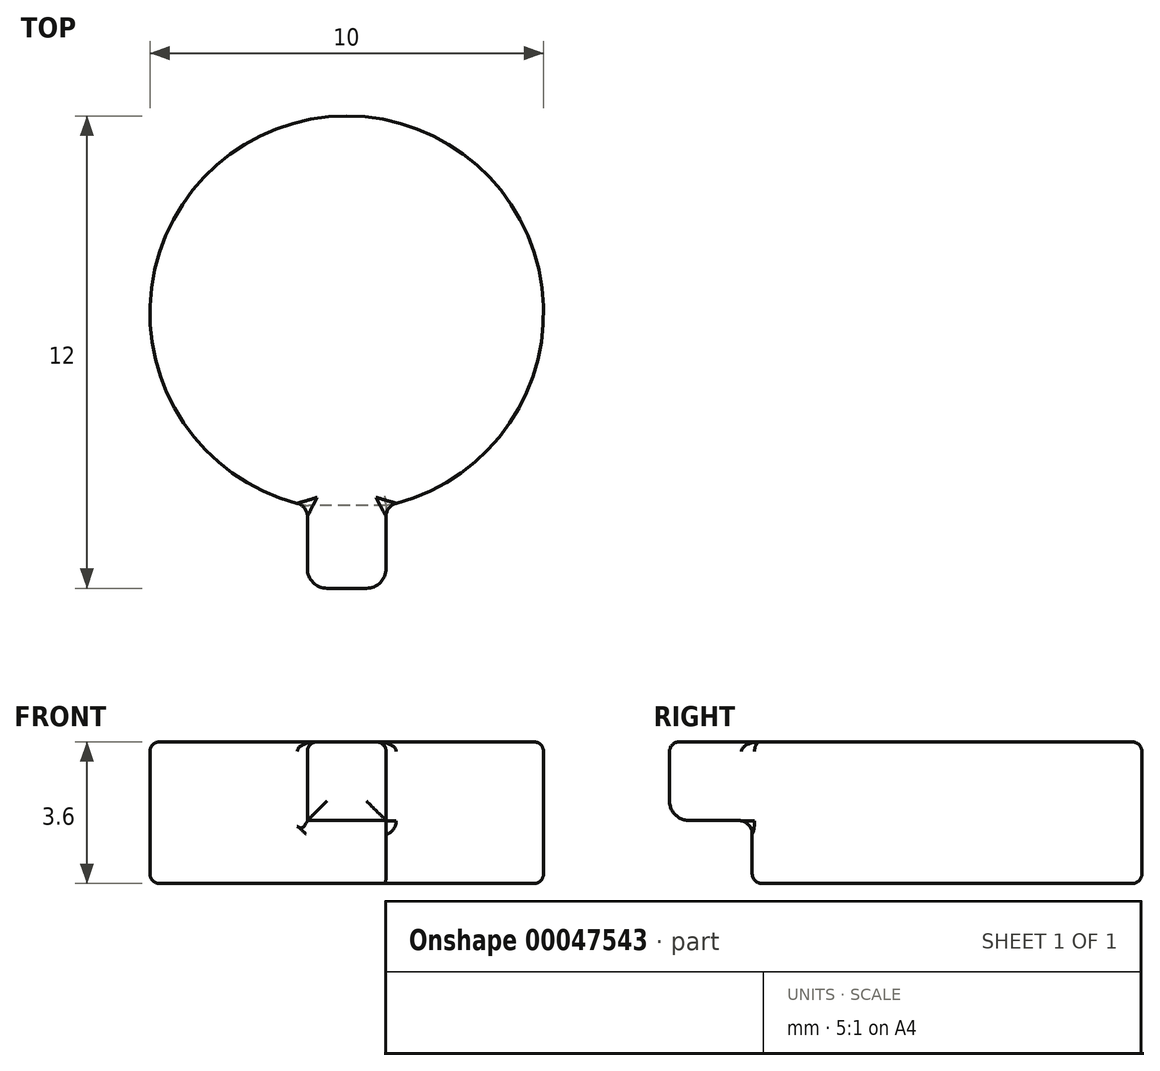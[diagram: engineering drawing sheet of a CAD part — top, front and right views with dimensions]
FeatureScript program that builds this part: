
annotation { "Feature Type Name" : "Feature", "Feature Type Description" : "" }
export const myFeature = defineFeature(function(context is Context, id is Id, definition is map)
    precondition{}
    {
        {
            var Q0;
            Q0=qCreatedBy(makeId("Top.planeOp"),FACE);
            var sketch = newSketch(context, id + "F0", { "sketchPlane" : qUnion([Q0])});
            skArc(sketch, "E0", {"start": v(1, -4.9) * mm, "mid": v(0, 5) * mm, "end": v(-1, -4.9) * mm});
            skLineSegment(sketch, "E1.top", {"start": v(-1, -7) * mm, "end": v(1, -7) * mm});
            skLineSegment(sketch, "E1.left", {"start": v(-1, -4.9) * mm, "end": v(-1, -7) * mm});
            skLineSegment(sketch, "E1.right", {"start": v(1, -4.9) * mm, "end": v(1, -7) * mm});
            skSolve(sketch);
        }
        {
            var Q0;
            Q0 = qSketchRegion(id + "F0", true);
            extrude(context, id + "F1", {"entities" : qUnion([Q0]), "depth" : 3.6 * mm});
        }
        {
            var Q0;
            Q0=makeQuery(id+"F1.opExtrude","SWEPT_FACE",FACE,{"disambiguationData":[OSD([sQuery(id+"F0.wireOp",EDGE,"E1.left")])]});
            var sketch = newSketch(context, id + "F2", { "sketchPlane" : qUnion([Q0])});
            skLineSegment(sketch, "E2.bottom", {"start": v(4.9, 0) * mm, "end": v(7, 0) * mm});
            skLineSegment(sketch, "E2.top", {"start": v(4.9, 1.6) * mm, "end": v(7, 1.6) * mm});
            skLineSegment(sketch, "E2.left", {"start": v(4.9, 0) * mm, "end": v(4.9, 1.6) * mm});
            skLineSegment(sketch, "E2.right", {"start": v(7, 0) * mm, "end": v(7, 1.6) * mm});
            skSolve(sketch);
        }
        {
            var Q0;
            Q0 = qSketchRegion(id + "F2", true);
            extrude(context, id + "F3", {"entities" : qUnion([Q0]), "operationType" : NewBodyOperationType.REMOVE, "oppositeDirection" : true, "depth" : 25 * mm});
        }
        {
            var Q0;
            Q0=makeQuery(id+"F1.opExtrude","CAP_FACE",FACE,{"disambiguationData":[OSD([sQuery(id+"F0.wireOp",EDGE,"E0"),sQuery(id+"F0.wireOp",EDGE,"E1.top"),sQuery(id+"F0.wireOp",EDGE,"E1.left"),sQuery(id+"F0.wireOp",EDGE,"E1.right")])],"isStart":false});
            var Q1;
            Q1=makeQuery(id+"F1.opExtrude","CAP_FACE",FACE,{"disambiguationData":[OSD([sQuery(id+"F0.wireOp",EDGE,"E0"),sQuery(id+"F0.wireOp",EDGE,"E1.top"),sQuery(id+"F0.wireOp",EDGE,"E1.left"),sQuery(id+"F0.wireOp",EDGE,"E1.right")])],"isStart":true});
            fillet(context, id + "F4", {"entities" : qUnion([Q0, Q1]), "radius" : .25 * mm, "tangentPropagation" : true, "allowEdgeOverflow" : false});
        }
        {
            var Q0;
            Q0=makeQuery(id+"F1.opExtrude","SWEPT_FACE",FACE,{"disambiguationData":[OSD([sQuery(id+"F0.wireOp",EDGE,"E1.top")])]});
            fillet(context, id + "F5", {"entities" : qUnion([Q0]), "radius" : .5 * mm, "tangentPropagation" : true, "allowEdgeOverflow" : false});
        }
        {
            var Q0;
            Q0=makeQuery(id+"F3.boolean.opBoolean","COPY",EDGE,{"derivedFrom":makeQuery(id+"F3.opExtrude","SWEPT_EDGE",EDGE,{"disambiguationData":[OSD([sQuery(id+"F0.wireOp",EDGE,"E0"),sQuery(id+"F0.wireOp",EDGE,"E1.left"),sQuery(id+"F2.wireOp",EDGE,"E2.top"),sQuery(id+"F2.wireOp",EDGE,"E2.left")])]})});
            var Q1;
            Q1=makeQuery(id+"F1.opExtrude","SWEPT_EDGE",EDGE,{"disambiguationData":[OSD([sQuery(id+"F0.wireOp",EDGE,"E0"),sQuery(id+"F0.wireOp",EDGE,"E1.left")])]});
            fillet(context, id + "F6", {"entities" : qUnion([Q0, Q1]), "radius" : 0.34 * mm, "tangentPropagation" : true, "allowEdgeOverflow" : false});
        }
        {
            var Q0;
            {var subQ0=sQuery(id+"F0.wireOp",EDGE,"E1.right");var subQ1=sQuery(id+"F0.wireOp",EDGE,"E0");Q0=makeQuery(id+"F3.boolean.opBoolean","SPLIT",EDGE,{"disambiguationData":[TD([makeQuery(id+"F1.opExtrude","CAP_FACE",FACE,{"disambiguationData":[OSD([subQ1,sQuery(id+"F0.wireOp",EDGE,"E1.top"),sQuery(id+"F0.wireOp",EDGE,"E1.left"),subQ0])],"isStart":false})])],"derivedFrom":makeQuery(id+"F1.opExtrude","SWEPT_EDGE",EDGE,{"disambiguationData":[OSD([subQ1,subQ0])]})});}
            fillet(context, id + "F7", {"entities" : qUnion([Q0]), "radius" : 0.34 * mm, "tangentPropagation" : true, "allowEdgeOverflow" : false});
        }
    });
